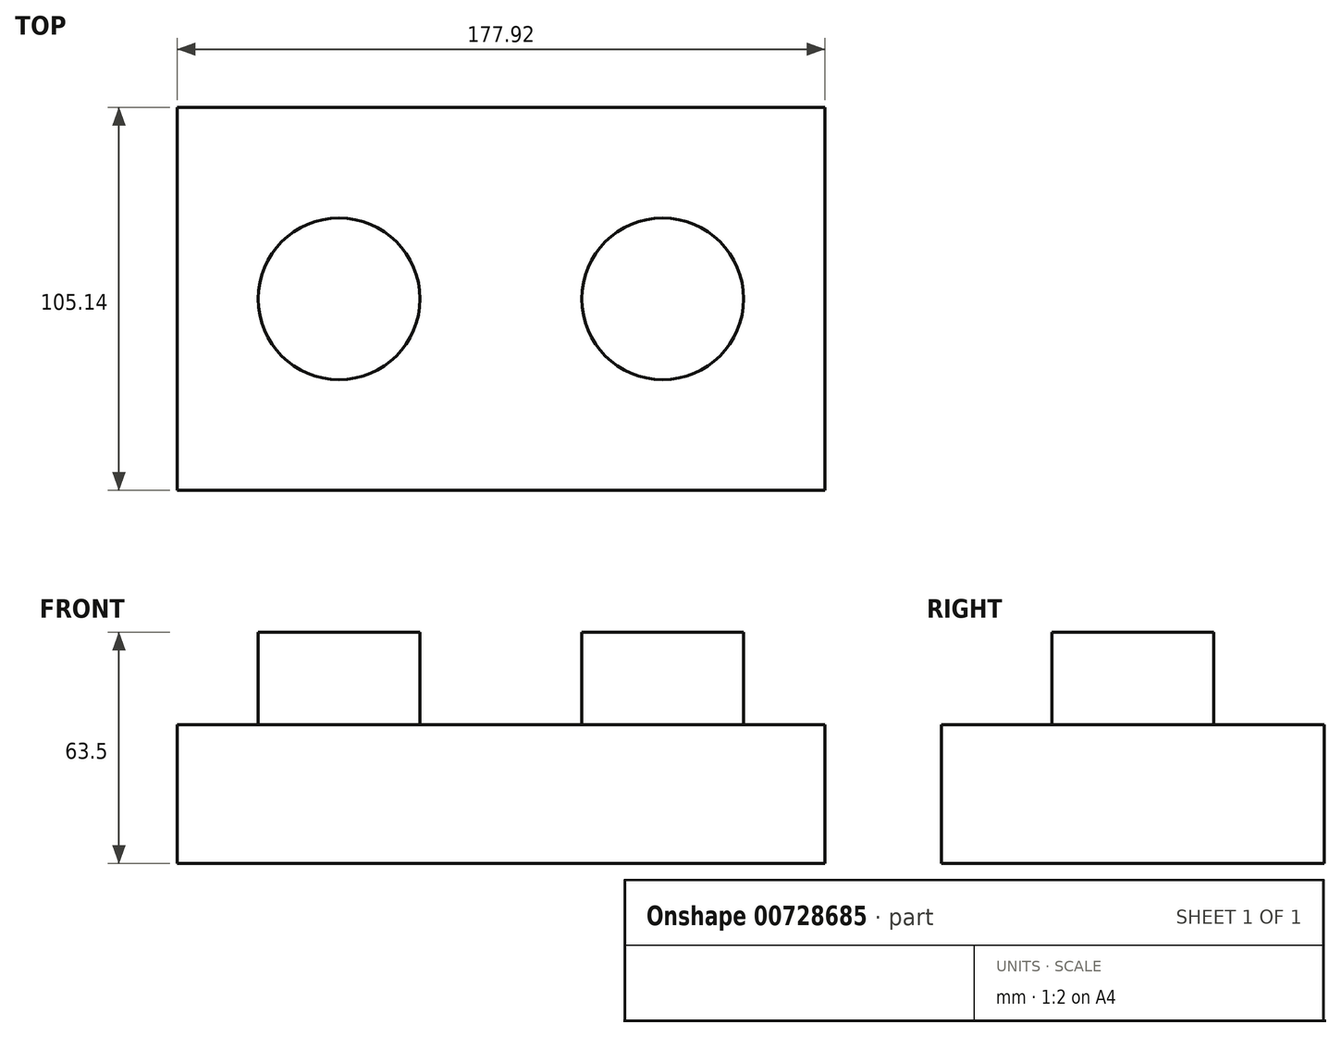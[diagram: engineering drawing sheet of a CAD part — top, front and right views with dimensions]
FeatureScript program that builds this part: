
annotation { "Feature Type Name" : "Feature", "Feature Type Description" : "" }
export const myFeature = defineFeature(function(context is Context, id is Id, definition is map)
    precondition{}
    {
        {
            var Q0;
            Q0=qCreatedBy(makeId("Top.planeOp"),FACE);
            var sketch = newSketch(context, id + "F0", { "sketchPlane" : qUnion([Q0])});
            skLineSegment(sketch, "E0.bottom", {"start": v(88.96, -52.57) * mm, "end": v(-88.96, -52.57) * mm});
            skLineSegment(sketch, "E0.top", {"start": v(88.96, 52.57) * mm, "end": v(-88.96, 52.57) * mm});
            skLineSegment(sketch, "E0.left", {"start": v(88.96, -52.57) * mm, "end": v(88.96, 52.57) * mm});
            skLineSegment(sketch, "E0.right", {"start": v(-88.96, -52.57) * mm, "end": v(-88.96, 52.57) * mm});
            skPoint(sketch, "E0.middle", {"position": v(0, 0) * mm});
            skSolve(sketch);
        }
        {
            var Q0;
            Q0 = qSketchRegion(id + "F0", true);
            extrude(context, id + "F1", {"entities" : qUnion([Q0]), "depth" : 38.1 * mm, "offsetDistance" : 25.4 * mm, "symmetric" : true});
        }
        {
            var Q0;
            Q0=makeQuery(id+"F1.opExtrude","CAP_FACE",FACE,{"disambiguationData":[OSD([sQuery(id+"F0.wireOp",EDGE,"E0.bottom"),sQuery(id+"F0.wireOp",EDGE,"E0.top"),sQuery(id+"F0.wireOp",EDGE,"E0.left"),sQuery(id+"F0.wireOp",EDGE,"E0.right")])],"isStart":false});
            var sketch = newSketch(context, id + "F2", { "sketchPlane" : qUnion([Q0])});
            skCircle(sketch, "E1", {"center": v(-44.5, 0) * mm, "radius": 22.23 * mm});
            skCircle(sketch, "E2", {"center": v(44.4, 0) * mm, "radius": 22.23 * mm});
            skSolve(sketch);
        }
        {
            var Q0;
            Q0 = qSketchRegion(id + "F2", true);
            extrude(context, id + "F3", {"entities" : qUnion([Q0]), "operationType" : NewBodyOperationType.ADD, "depth" : 25.4 * mm, "offsetDistance" : 25.4 * mm});
        }
    });
